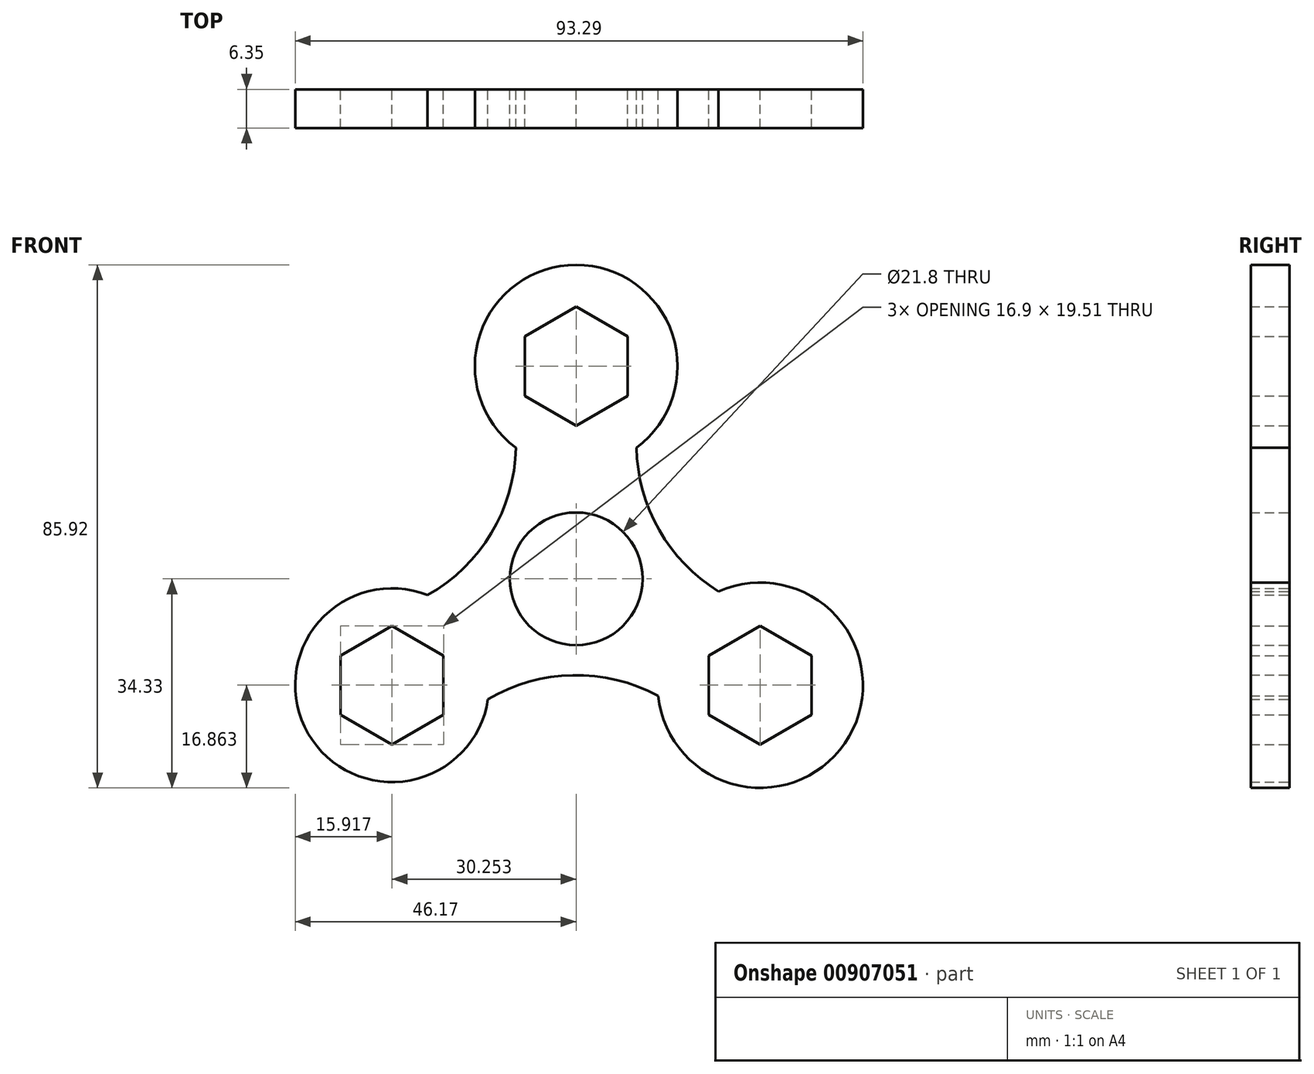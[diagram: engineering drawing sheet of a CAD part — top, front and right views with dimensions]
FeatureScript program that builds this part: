
annotation { "Feature Type Name" : "Feature", "Feature Type Description" : "" }
export const myFeature = defineFeature(function(context is Context, id is Id, definition is map)
    precondition{}
    {
        {
            var Q0;
            Q0=qCreatedBy(makeId("Front.planeOp"),FACE);
            var sketch = newSketch(context, id + "F0", { "sketchPlane" : qUnion([Q0])});
            skCircle(sketch, "E0", {"center": v(0, 0) * mm, "radius": 10.9 * mm});
            skCircle(sketch, "E1.cCircle", {"center": v(0, 34.93) * mm, "radius": 8.45 * mm, "construction": true});
            skLineSegment(sketch, "E1.0", {"start": v(8.45, 39.81) * mm, "end": v(8.45, 30.05) * mm});
            skLineSegment(sketch, "E1.1", {"start": v(8.45, 30.05) * mm, "end": v(0, 25.18) * mm});
            skLineSegment(sketch, "E1.2", {"start": v(0, 25.18) * mm, "end": v(-8.45, 30.05) * mm});
            skLineSegment(sketch, "E1.3", {"start": v(-8.45, 30.05) * mm, "end": v(-8.45, 39.81) * mm});
            skLineSegment(sketch, "E1.4", {"start": v(-8.45, 39.81) * mm, "end": v(0, 44.7) * mm});
            skLineSegment(sketch, "E1.5", {"start": v(0, 44.7) * mm, "end": v(8.45, 39.81) * mm});
            skPoint(sketch, "E1.0.midPoint", {"position": v(8.45, 34.93) * mm});
            skCircle(sketch, "E2.1.1", {"center": v(-30.25, -17.47) * mm, "radius": 8.45 * mm, "construction": true});
            skPoint(sketch, "E2.1.2", {"position": v(-34.48, -10.15) * mm});
            skLineSegment(sketch, "E2.1.3", {"start": v(-21.8, -22.35) * mm, "end": v(-30.25, -27.22) * mm});
            skLineSegment(sketch, "E2.1.4", {"start": v(-38.7, -12.59) * mm, "end": v(-30.25, -7.7) * mm});
            skLineSegment(sketch, "E2.1.5", {"start": v(-38.7, -22.35) * mm, "end": v(-38.7, -12.59) * mm});
            skLineSegment(sketch, "E2.1.6", {"start": v(-30.25, -27.22) * mm, "end": v(-38.7, -22.35) * mm});
            skLineSegment(sketch, "E2.1.7", {"start": v(-21.8, -12.59) * mm, "end": v(-21.8, -22.35) * mm});
            skLineSegment(sketch, "E2.1.8", {"start": v(-30.25, -7.7) * mm, "end": v(-21.8, -12.59) * mm});
            skCircle(sketch, "E2.2.1", {"center": v(30.25, -17.47) * mm, "radius": 8.45 * mm, "construction": true});
            skPoint(sketch, "E2.2.2", {"position": v(26.03, -24.78) * mm});
            skLineSegment(sketch, "E2.2.3", {"start": v(30.25, -7.7) * mm, "end": v(38.7, -12.59) * mm});
            skLineSegment(sketch, "E2.2.4", {"start": v(30.25, -27.22) * mm, "end": v(21.8, -22.35) * mm});
            skLineSegment(sketch, "E2.2.5", {"start": v(38.7, -22.35) * mm, "end": v(30.25, -27.22) * mm});
            skLineSegment(sketch, "E2.2.6", {"start": v(38.7, -12.59) * mm, "end": v(38.7, -22.35) * mm});
            skLineSegment(sketch, "E2.2.7", {"start": v(21.8, -12.59) * mm, "end": v(30.25, -7.7) * mm});
            skLineSegment(sketch, "E2.2.8", {"start": v(21.8, -22.35) * mm, "end": v(21.8, -12.59) * mm});
            skArc(sketch, "E3", {"start": v(13.48, -19.23) * mm, "mid": v(-0.59, -15.83) * mm, "end": v(-14.5, -19.82) * mm});
            skArc(sketch, "E4.1.0", {"start": v(9.91, 21.55) * mm, "mid": v(13.64, 8.02) * mm, "end": v(23.4, -2.06) * mm});
            skArc(sketch, "E4.2.0", {"start": v(-24.42, -2.65) * mm, "mid": v(-13.94, 7.51) * mm, "end": v(-9.91, 21.55) * mm});
            skArc(sketch, "E5", {"start": v(-24.42, -2.65) * mm, "mid": v(-44.04, -25.43) * mm, "end": v(-14.5, -19.82) * mm});
            skPoint(sketch, "E6.orphan", {"position": v(-18.08, -22.35) * mm});
            skArc(sketch, "E7", {"start": v(9.91, 21.55) * mm, "mid": v(0, 51.59) * mm, "end": v(-9.91, 21.55) * mm});
            skPoint(sketch, "E8.orphan", {"position": v(-10.3, 26.83) * mm});
            skPoint(sketch, "E9.orphan", {"position": v(10.3, 26.83) * mm});
            skArc(sketch, "E10", {"start": v(13.48, -19.23) * mm, "mid": v(44.86, -25.9) * mm, "end": v(23.4, -2.06) * mm});
            skPoint(sketch, "E11.orphan", {"position": v(18.08, -22.35) * mm});
            skPoint(sketch, "E12.orphan", {"position": v(28.4, -4.49) * mm});
            skSolve(sketch);
        }
        {
            var Q0;
            Q0=makeQuery(id+"F0.imprint","IMPRINT",FACE,{"disambiguationData":[TD([[makeQuery(id+"F0.imprint","IMPRINT",EDGE,{"derivedFrom":sQuery(id+"F0.wireOp",EDGE,"E0")}),-1.0]])]});
            var Q1;
            Q1=makeQuery(id+"F0.imprint","IMPRINT",FACE,{"disambiguationData":[TD([[makeQuery(id+"F0.imprint","IMPRINT",EDGE,{"derivedFrom":sQuery(id+"F0.wireOp",EDGE,"E2.1.3")}),1.0]])]});
            var Q2;
            Q2=makeQuery(id+"F0.imprint","IMPRINT",FACE,{"disambiguationData":[TD([[makeQuery(id+"F0.imprint","IMPRINT",EDGE,{"derivedFrom":sQuery(id+"F0.wireOp",EDGE,"E2.2.3")}),1.0]])]});
            var Q3;
            Q3=makeQuery(id+"F0.imprint","IMPRINT",FACE,{"disambiguationData":[TD([[makeQuery(id+"F0.imprint","IMPRINT",EDGE,{"derivedFrom":sQuery(id+"F0.wireOp",EDGE,"E1.0")}),1.0]])]});
            extrude(context, id + "F1", {"entities" : qUnion([Q0, Q1, Q2, Q3]), "depth" : 6.35 * mm, "offsetDistance" : 25.4 * mm});
        }
    });
